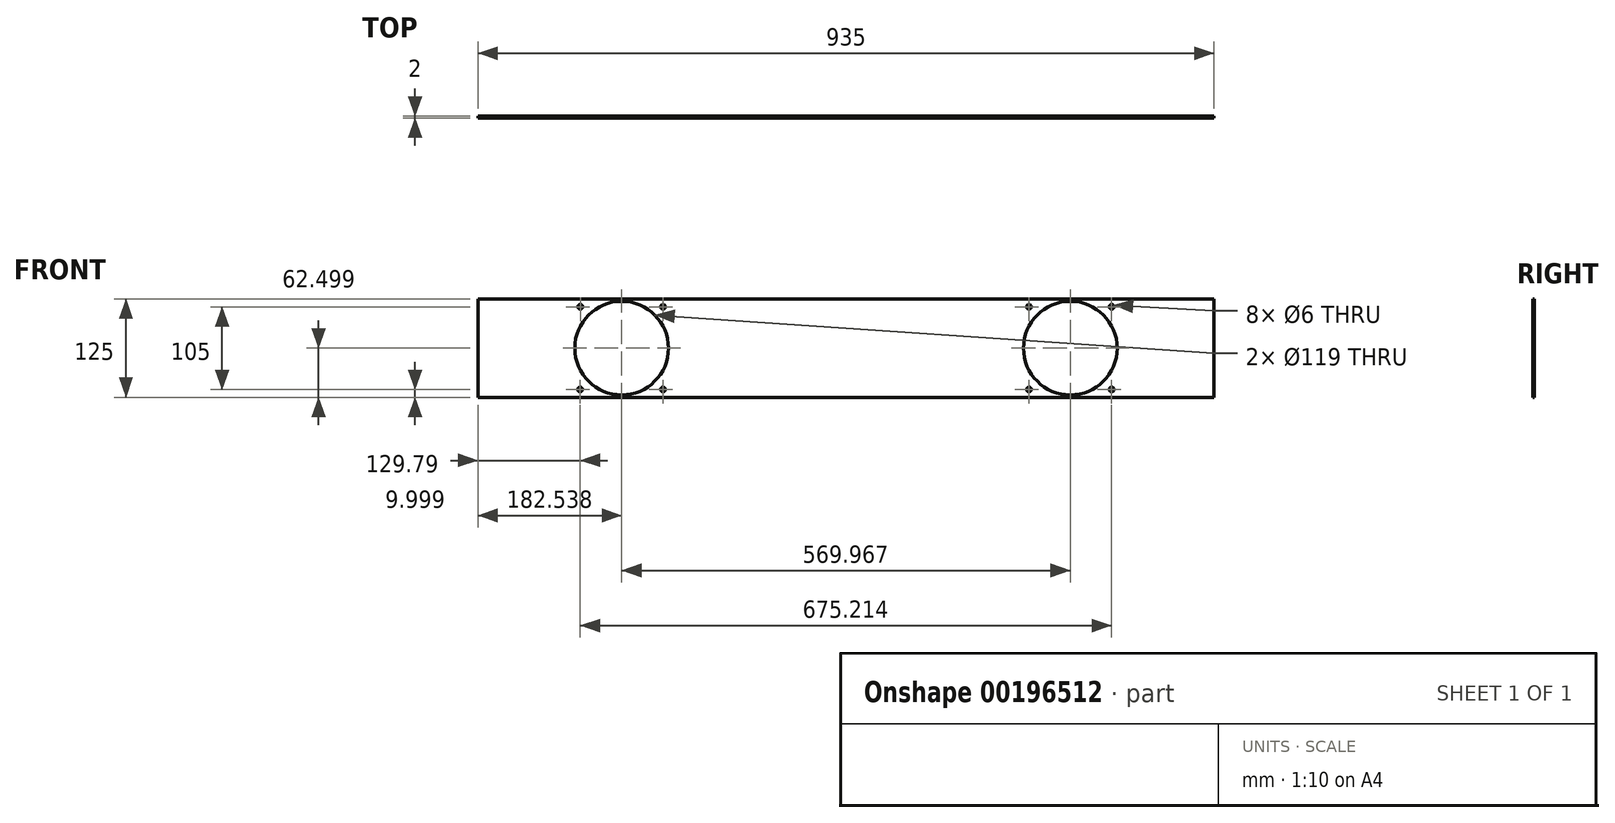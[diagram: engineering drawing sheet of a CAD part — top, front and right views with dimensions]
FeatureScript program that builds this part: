
annotation { "Feature Type Name" : "Feature", "Feature Type Description" : "" }
export const myFeature = defineFeature(function(context is Context, id is Id, definition is map)
    precondition{}
    {
        {
            var Q0;
            Q0=qCreatedBy(makeId("Front.planeOp"),FACE);
            var sketch = newSketch(context, id + "F0", { "sketchPlane" : qUnion([Q0])});
            skLineSegment(sketch, "E0", {"start": v(-131.28, 41.3) * mm, "end": v(803.72, 41.3) * mm});
            skLineSegment(sketch, "E1", {"start": v(803.72, 41.3) * mm, "end": v(803.72, -83.7) * mm});
            skLineSegment(sketch, "E2", {"start": v(803.72, -83.7) * mm, "end": v(-131.28, -83.7) * mm});
            skLineSegment(sketch, "E3", {"start": v(-131.28, -83.7) * mm, "end": v(-131.28, 41.3) * mm});
            skPoint(sketch, "E4", {"position": v(-1.24, 31.3) * mm});
            skPoint(sketch, "E5", {"position": v(-1.5, -73.7) * mm});
            skCircle(sketch, "E6", {"center": v(-1.5, -73.7) * mm, "radius": 3 * mm});
            skPoint(sketch, "E7", {"position": v(103.76, 31.3) * mm});
            skCircle(sketch, "E8", {"center": v(103.76, 31.3) * mm, "radius": 3 * mm});
            skCircle(sketch, "E9", {"center": v(-1.5, -182.8) * mm, "radius": 3 * mm});
            skPoint(sketch, "E10", {"position": v(-1.24, 132.2) * mm});
            skPoint(sketch, "E11", {"position": v(103.76, -73.7) * mm});
            skCircle(sketch, "E12", {"center": v(103.76, -73.7) * mm, "radius": 3 * mm});
            skCircle(sketch, "E13", {"center": v(-1.24, 31.3) * mm, "radius": 3 * mm});
            skPoint(sketch, "E14", {"position": v(568.72, 31.3) * mm});
            skPoint(sketch, "E15", {"position": v(673.72, 31.3) * mm});
            skPoint(sketch, "E16", {"position": v(568.72, -73.7) * mm});
            skPoint(sketch, "E17", {"position": v(673.72, -73.7) * mm});
            skPoint(sketch, "E18", {"position": v(51.26, -21.2) * mm});
            skCircle(sketch, "E19", {"center": v(51.26, -21.2) * mm, "radius": 59.5 * mm});
            skPoint(sketch, "E20", {"position": v(621.22, -21.2) * mm});
            skCircle(sketch, "E21", {"center": v(621.22, -21.2) * mm, "radius": 59.5 * mm});
            skCircle(sketch, "E22", {"center": v(568.72, 31.3) * mm, "radius": 3 * mm});
            skCircle(sketch, "E23", {"center": v(673.72, 31.3) * mm, "radius": 3 * mm});
            skCircle(sketch, "E24", {"center": v(673.72, -73.7) * mm, "radius": 3 * mm});
            skCircle(sketch, "E25", {"center": v(568.72, -73.7) * mm, "radius": 3 * mm});
            skSolve(sketch);
        }
        {
            var Q0;
            Q0=makeQuery(id+"F0.imprint","IMPRINT",FACE,{"disambiguationData":[TD([[makeQuery(id+"F0.imprint","IMPRINT",EDGE,{"derivedFrom":sQuery(id+"F0.wireOp",EDGE,"E0")}),-1.0]])]});
            extrude(context, id + "F1", {"entities" : qUnion([Q0]), "depth" : 2 * mm});
        }
    });
